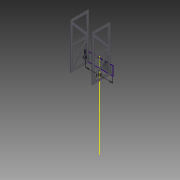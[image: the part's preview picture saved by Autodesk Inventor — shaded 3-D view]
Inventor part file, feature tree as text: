
AUTODESK INVENTOR PART (.ipt)
format: ipt  version: 2017 (Build 210142000, 142)  size: 189,952 bytes
history: native  units: mm
features: sketch x5, other x4, reference x4, hole x3, extrude x2, sheet_metal_op x1, plane x1
ambient origin geometry x8: Origin, YZ Plane, XZ Plane, XY Plane, X Axis, Y Axis, Z Axis, Center Point
bodies: Solid1 (feature_tree)
feature tree (20):
  sketch  "Sketch1"  dims[d0=180.0mm d2=3.0mm]
  sheet_metal_op  "Face1"
  hole  "Hole1"  [1 undecoded]
  plane  "Work Plane1"
  hole  "Hole3"  [1 undecoded]
  extrude  "Extrusion3"  Depth=60.0mm
  sketch  "Sketch10"  dims[d56=10.0mm d57=5.0mm d58=4.0mm d59=6.0mm d60=4.0mm d61=2.0mm d62=90.0deg d63=3.0mm d64=20.594885mm d65=3.0mm d66=140.0mm d67=120.0mm d68=260.0mm d69=0.0mm d70=15.0mm d71=15.0mm d72=15.0mm d73=15.0mm d74=15.0mm d75=15.0mm d77=15.0mm d78=300.0mm d79=0.0mm d80=8.0mm d81=8.0mm d82=8.0mm d83=8.0mm d84=4.0mm d85=6.0mm d86=4.0mm d87=2.0mm d88=90.0deg d89=3.0mm d90=20.594885mm]
  extrude  "Extrusion4"  Depth=3.0mm
  hole  "Hole4"  [1 undecoded]
  other  "Plate1"
  sketch  "Sketch2"  dims[d4=8.2mm]
  reference  "Reference3"
  reference  "Reference4"
  reference  "Reference5"
  reference  "Reference6"
  sketch  "Sketch8"  dims[d5=4.0mm d6=6.0mm d7=4.0mm d8=2.0mm d9=90.0deg d10=3.0mm d11=20.594885mm]
  sketch  "Sketch9"  dims[d31=86.0mm d34=60.0mm]
  parser-record x1  (decoder bookkeeping rows leaked as tree rows — omitted from the tree; the rows remain in map.json)
  other  "Balloon Assembly.iam"
  other  "LENS MOUNT:1"
note: 3 required parameter values undecoded (feature->parameter linkage not recoverable at this tier; creation-order binding heuristic only, values carry confidence <= 0.55)
note: 1 file-system path scrubbed to <path> (originals preserved in map.json)
